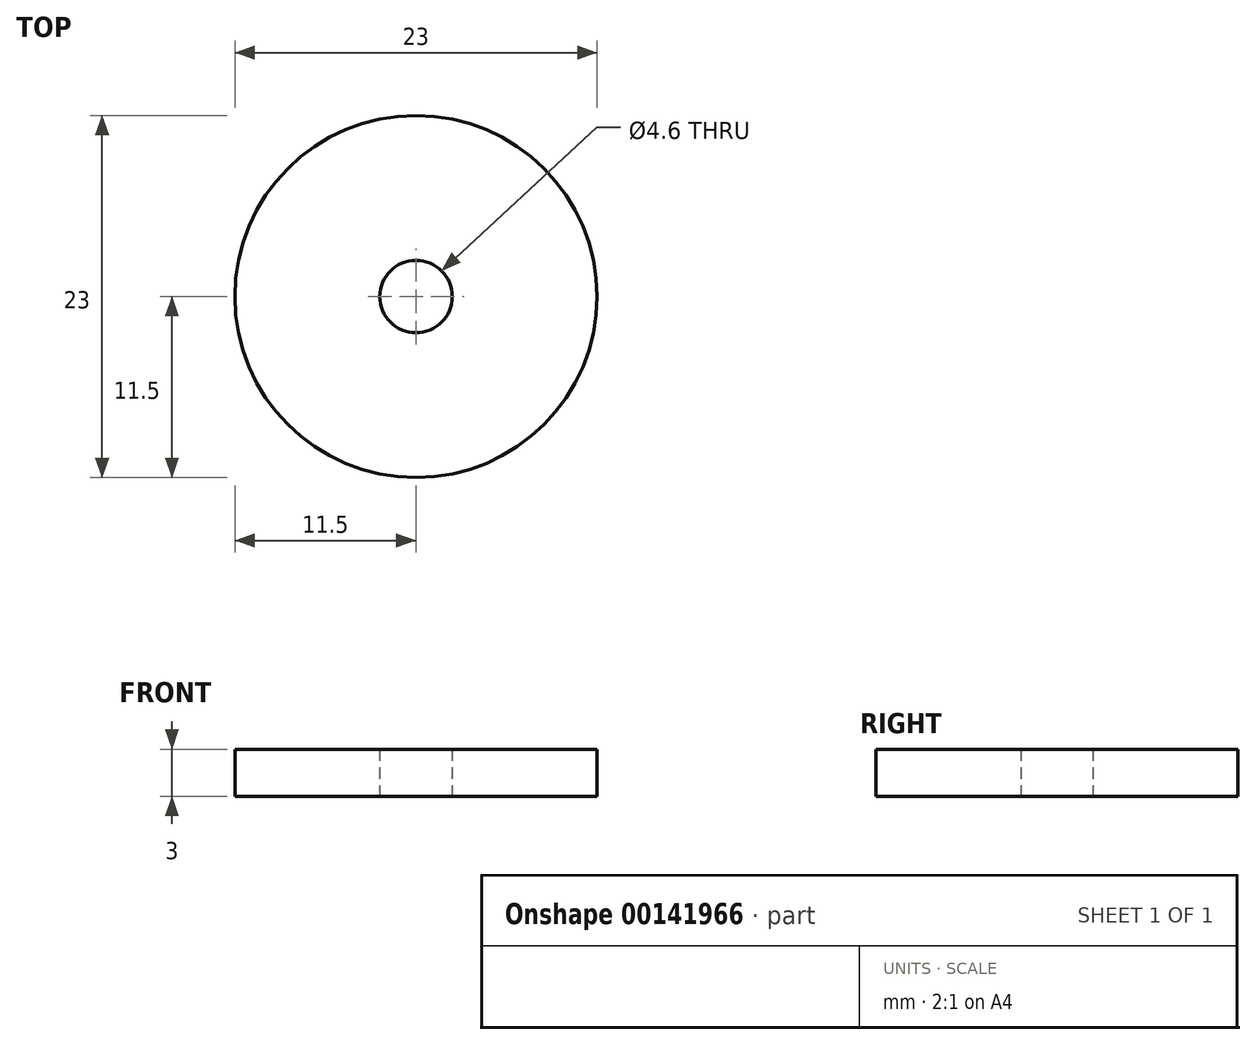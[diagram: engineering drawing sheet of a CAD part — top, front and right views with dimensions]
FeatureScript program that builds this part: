
annotation { "Feature Type Name" : "Feature", "Feature Type Description" : "" }
export const myFeature = defineFeature(function(context is Context, id is Id, definition is map)
    precondition{}
    {
        {
            var Q0;
            Q0=qCreatedBy(makeId("Top.planeOp"),FACE);
            var sketch = newSketch(context, id + "F0", { "sketchPlane" : qUnion([Q0])});
            skCircle(sketch, "E0", {"center": v(0, 0) * mm, "radius": 11.5 * mm});
            skCircle(sketch, "E1", {"center": v(0, 0) * mm, "radius": 2.3 * mm});
            skSolve(sketch);
        }
        {
            var Q0;
            Q0=makeQuery(id+"F0.imprint","IMPRINT",FACE,{"disambiguationData":[TD([[makeQuery(id+"F0.imprint","IMPRINT",EDGE,{"derivedFrom":sQuery(id+"F0.wireOp",EDGE,"E0")}),1.0]])]});
            extrude(context, id + "F1", {"entities" : qUnion([Q0]), "depth" : 3 * mm});
        }
    });
